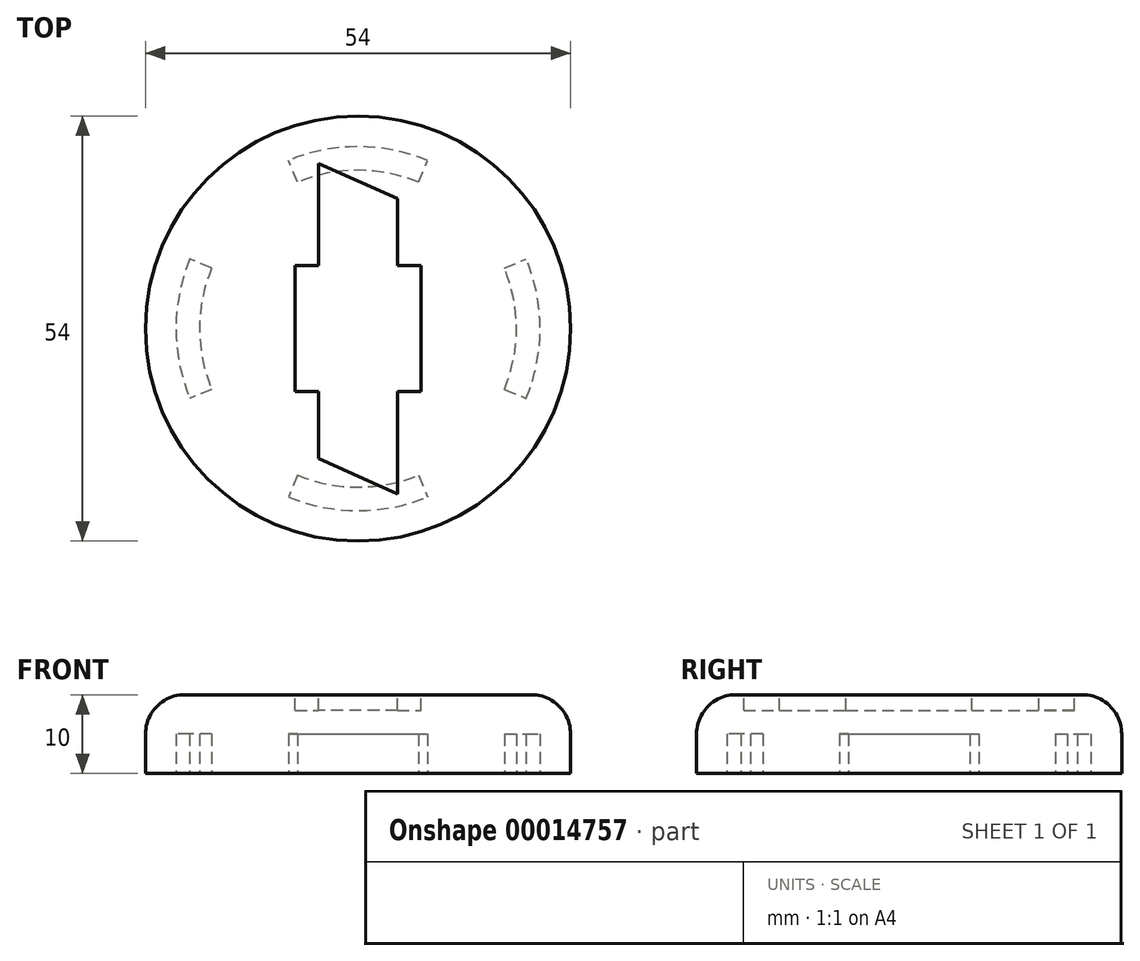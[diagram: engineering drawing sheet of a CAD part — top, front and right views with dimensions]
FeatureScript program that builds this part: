
annotation { "Feature Type Name" : "Feature", "Feature Type Description" : "" }
export const myFeature = defineFeature(function(context is Context, id is Id, definition is map)
    precondition{}
    {
        {
            var Q0;
            Q0=qCreatedBy(makeId("Top.planeOp"),FACE);
            var sketch = newSketch(context, id + "F0", { "sketchPlane" : qUnion([Q0])});
            skCircle(sketch, "E0", {"center": v(0, 0) * mm, "radius": 27 * mm});
            skSolve(sketch);
        }
        {
            var Q0;
            Q0=makeQuery(id+"F0.imprint","IMPRINT",FACE,{"disambiguationData":[TD([[makeQuery(id+"F0.imprint","IMPRINT",EDGE,{"derivedFrom":sQuery(id+"F0.wireOp",EDGE,"E0")}),1.0]])]});
            extrude(context, id + "F1", {"entities" : qUnion([Q0]), "depth" : 10 * mm});
        }
        {
            var Q0;
            Q0=makeQuery(id+"F1.opExtrude","CAP_EDGE",EDGE,{"disambiguationData":[OSD([sQuery(id+"F0.wireOp",EDGE,"E0")])],"isStart":false});
            fillet(context, id + "F2", {"entities" : qUnion([Q0]), "radius" : 5 * mm, "tangentPropagation" : true, "allowEdgeOverflow" : false});
        }
        {
            var Q0;
            Q0=makeQuery(id+"F1.opExtrude","CAP_FACE",FACE,{"disambiguationData":[OSD([sQuery(id+"F0.wireOp",EDGE,"E0")])],"isStart":false});
            cPlane(context, id + "F3", {"entities" : qUnion([Q0]), "cplaneType" : CPlaneType.OFFSET, "offset" : 0 * mm, "width" : 150 * mm, "height" : 150 * mm});
        }
        {
            var Q0;
            Q0=qCreatedBy(id+"F3.planeOp",FACE);
            var sketch = newSketch(context, id + "F4", { "sketchPlane" : qUnion([Q0])});
            skLineSegment(sketch, "E1.left", {"start": v(-5, -16.5) * mm, "end": v(-5, -8) * mm});
            skLineSegment(sketch, "E1.right", {"start": v(5, -21) * mm, "end": v(5, -8) * mm});
            skLineSegment(sketch, "E2.bottom", {"start": v(-8, -8) * mm, "end": v(-5, -8) * mm});
            skLineSegment(sketch, "E2.top", {"start": v(-8, 8) * mm, "end": v(-5, 8) * mm});
            skLineSegment(sketch, "E2.left", {"start": v(-8, -8) * mm, "end": v(-8, 8) * mm});
            skLineSegment(sketch, "E2.right", {"start": v(8, -8) * mm, "end": v(8, 8) * mm});
            skLineSegment(sketch, "E3", {"start": v(5, -21) * mm, "end": v(-5, -16.5) * mm});
            skLineSegment(sketch, "E4", {"start": v(-5, 21) * mm, "end": v(5, 16.5) * mm});
            skLineSegment(sketch, "E5.trimOffspring", {"start": v(5, -8) * mm, "end": v(8, -8) * mm});
            skLineSegment(sketch, "E6.trimOffspring", {"start": v(-5, 8) * mm, "end": v(-5, 21) * mm});
            skLineSegment(sketch, "E7.trimOffspring", {"start": v(5, 8) * mm, "end": v(8, 8) * mm});
            skLineSegment(sketch, "E8.trimOffspring", {"start": v(5, 8) * mm, "end": v(5, 16.5) * mm});
            skSolve(sketch);
        }
        {
            var Q0;
            Q0=makeQuery(id+"F4.imprint","IMPRINT",FACE,{"disambiguationData":[TD([[makeQuery(id+"F4.imprint","IMPRINT",EDGE,{"derivedFrom":sQuery(id+"F4.wireOp",EDGE,"E1.left")}),-1.0]])]});
            extrude(context, id + "F5", {"entities" : qUnion([Q0]), "operationType" : NewBodyOperationType.REMOVE, "oppositeDirection" : true, "depth" : 2 * mm});
        }
        {
            var Q0;
            Q0=makeQuery(id+"F1.opExtrude","CAP_FACE",FACE,{"disambiguationData":[OSD([sQuery(id+"F0.wireOp",EDGE,"E0")])],"isStart":true});
            cPlane(context, id + "F6", {"entities" : qUnion([Q0]), "cplaneType" : CPlaneType.OFFSET, "offset" : 0 * mm, "width" : 150 * mm, "height" : 150 * mm});
        }
        {
            var Q0;
            Q0=qCreatedBy(id+"F6.planeOp",FACE);
            var sketch = newSketch(context, id + "F7", { "sketchPlane" : qUnion([Q0])});
            skArc(sketch, "E9", {"start": v(8.85, 21.36) * mm, "mid": v(0, 23.12) * mm, "end": v(-8.85, 21.36) * mm});
            skArc(sketch, "E10", {"start": v(7.7, 18.6) * mm, "mid": v(0, 20.12) * mm, "end": v(-7.7, 18.6) * mm});
            skLineSegment(sketch, "E11", {"start": v(18.6, 7.7) * mm, "end": v(21.36, 8.85) * mm});
            skLineSegment(sketch, "E12", {"start": v(18.6, -7.7) * mm, "end": v(21.36, -8.85) * mm});
            skLineSegment(sketch, "E13", {"start": v(7.7, 18.6) * mm, "end": v(8.85, 21.36) * mm});
            skLineSegment(sketch, "E14", {"start": v(-7.7, 18.6) * mm, "end": v(-8.85, 21.36) * mm});
            skLineSegment(sketch, "E15", {"start": v(-18.6, 7.7) * mm, "end": v(-21.36, 8.85) * mm});
            skLineSegment(sketch, "E16", {"start": v(-18.6, -7.7) * mm, "end": v(-21.36, -8.85) * mm});
            skLineSegment(sketch, "E17", {"start": v(7.7, -18.6) * mm, "end": v(8.85, -21.36) * mm});
            skLineSegment(sketch, "E18", {"start": v(-7.7, -18.6) * mm, "end": v(-8.85, -21.36) * mm});
            skArc(sketch, "E19.trimOffspring", {"start": v(-18.6, 7.7) * mm, "mid": v(-20.12, 0) * mm, "end": v(-18.6, -7.7) * mm});
            skArc(sketch, "E20.trimOffspring", {"start": v(-21.36, 8.85) * mm, "mid": v(-23.13, 0) * mm, "end": v(-21.36, -8.85) * mm});
            skArc(sketch, "E21.trimOffspring", {"start": v(-7.7, -18.6) * mm, "mid": v(0, -20.12) * mm, "end": v(7.7, -18.6) * mm});
            skArc(sketch, "E22.trimOffspring", {"start": v(-8.85, -21.36) * mm, "mid": v(0, -23.12) * mm, "end": v(8.85, -21.36) * mm});
            skArc(sketch, "E23.trimOffspring", {"start": v(18.6, -7.7) * mm, "mid": v(20.12, 0) * mm, "end": v(18.6, 7.7) * mm});
            skArc(sketch, "E24.trimOffspring", {"start": v(21.36, -8.85) * mm, "mid": v(23.12, 0) * mm, "end": v(21.36, 8.85) * mm});
            skSolve(sketch);
        }
        {
            var Q0;
            Q0=makeQuery(id+"F7.imprint","IMPRINT",FACE,{"disambiguationData":[TD([[makeQuery(id+"F7.imprint","IMPRINT",EDGE,{"derivedFrom":sQuery(id+"F7.wireOp",EDGE,"E9")}),1.0]])]});
            var Q1;
            Q1=makeQuery(id+"F7.imprint","IMPRINT",FACE,{"disambiguationData":[TD([[makeQuery(id+"F7.imprint","IMPRINT",EDGE,{"derivedFrom":sQuery(id+"F7.wireOp",EDGE,"E11")}),-1.0]])]});
            var Q2;
            Q2=makeQuery(id+"F7.imprint","IMPRINT",FACE,{"disambiguationData":[TD([[makeQuery(id+"F7.imprint","IMPRINT",EDGE,{"derivedFrom":sQuery(id+"F7.wireOp",EDGE,"E17")}),-1.0]])]});
            var Q3;
            Q3=makeQuery(id+"F7.imprint","IMPRINT",FACE,{"disambiguationData":[TD([[makeQuery(id+"F7.imprint","IMPRINT",EDGE,{"derivedFrom":sQuery(id+"F7.wireOp",EDGE,"E15")}),1.0]])]});
            extrude(context, id + "F8", {"entities" : qUnion([Q0, Q1, Q2, Q3]), "operationType" : NewBodyOperationType.REMOVE, "oppositeDirection" : true, "depth" : 5 * mm});
        }
    });
